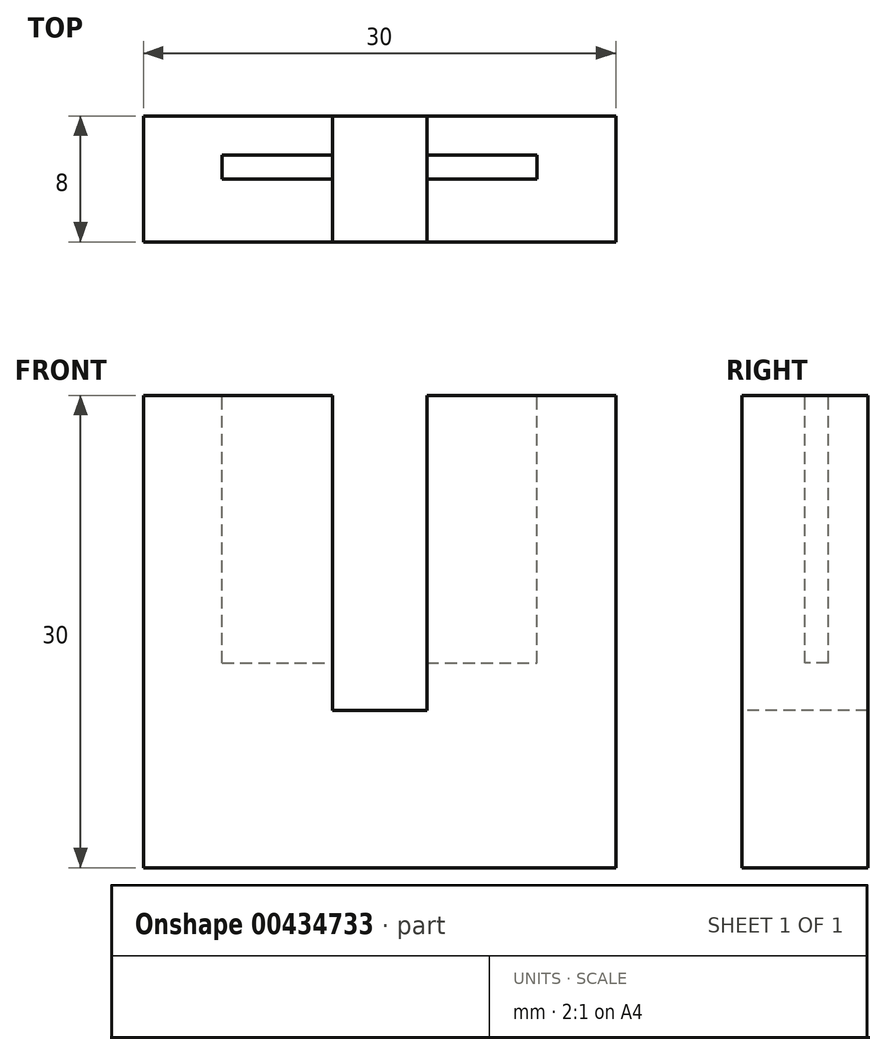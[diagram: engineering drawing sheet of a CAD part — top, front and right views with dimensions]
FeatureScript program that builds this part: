
annotation { "Feature Type Name" : "Feature", "Feature Type Description" : "" }
export const myFeature = defineFeature(function(context is Context, id is Id, definition is map)
    precondition{}
    {
        {
            var Q0;
            Q0=qCreatedBy(makeId("Top.planeOp"),FACE);
            var sketch = newSketch(context, id + "F0", { "sketchPlane" : qUnion([Q0])});
            skLineSegment(sketch, "E0.bottom", {"start": v(0, 0) * mm, "end": v(-30, 0) * mm});
            skLineSegment(sketch, "E0.top", {"start": v(0, -8) * mm, "end": v(-30, -8) * mm});
            skLineSegment(sketch, "E0.left", {"start": v(0, 0) * mm, "end": v(0, -8) * mm});
            skLineSegment(sketch, "E0.right", {"start": v(-30, 0) * mm, "end": v(-30, -8) * mm});
            skSolve(sketch);
        }
        {
            var Q0;
            Q0=makeQuery(id+"F0.imprint","IMPRINT",FACE,{"disambiguationData":[TD([[makeQuery(id+"F0.imprint","IMPRINT",EDGE,{"derivedFrom":sQuery(id+"F0.wireOp",EDGE,"E0.bottom")}),1.0]])]});
            extrude(context, id + "F1", {"entities" : qUnion([Q0]), "depth" : 30 * mm});
        }
        {
            var Q0;
            Q0=makeQuery(id+"F1.opExtrude","CAP_FACE",FACE,{"disambiguationData":[OSD([sQuery(id+"F0.wireOp",EDGE,"E0.bottom"),sQuery(id+"F0.wireOp",EDGE,"E0.top"),sQuery(id+"F0.wireOp",EDGE,"E0.left"),sQuery(id+"F0.wireOp",EDGE,"E0.right")])],"isStart":false});
            var sketch = newSketch(context, id + "F2", { "sketchPlane" : qUnion([Q0])});
            skLineSegment(sketch, "E1.bottom", {"start": v(-25, -2.5) * mm, "end": v(-5, -2.5) * mm});
            skLineSegment(sketch, "E1.top", {"start": v(-25, -4) * mm, "end": v(-5, -4) * mm});
            skLineSegment(sketch, "E1.left", {"start": v(-25, -2.5) * mm, "end": v(-25, -4) * mm});
            skLineSegment(sketch, "E1.right", {"start": v(-5, -2.5) * mm, "end": v(-5, -4) * mm});
            skSolve(sketch);
        }
        {
            var Q0;
            Q0=makeQuery(id+"F2.imprint","IMPRINT",FACE,{"disambiguationData":[TD([[makeQuery(id+"F2.imprint","IMPRINT",EDGE,{"derivedFrom":sQuery(id+"F2.wireOp",EDGE,"E1.bottom")}),1.0]])]});
            var sketch = newSketch(context, id + "F3", { "sketchPlane" : qUnion([Q0])});
            skLineSegment(sketch, "E2.bottom", {"start": v(-18, 0) * mm, "end": v(-12, 0) * mm});
            skLineSegment(sketch, "E2.top", {"start": v(-18, -8) * mm, "end": v(-12, -8) * mm});
            skLineSegment(sketch, "E2.left", {"start": v(-18, 0) * mm, "end": v(-18, -8) * mm});
            skLineSegment(sketch, "E2.right", {"start": v(-12, 0) * mm, "end": v(-12, -8) * mm});
            skSolve(sketch);
        }
        {
            var Q0;
            {var subQ0=sQuery(id+"F3.wireOp",EDGE,"E2.bottom");Q0=makeQuery(id+"F3.imprint","IMPRINT",FACE,{"disambiguationData":[TD([[makeQuery(id+"F3.imprint","IMPRINT",EDGE,{"derivedFrom":subQ0}),1.0]])]});}
            var Q1;
            {var subQ0=sQuery(id+"F3.wireOp",EDGE,"E2.left");var subQ1=makeQuery(id+"F2.imprint","IMPRINT",EDGE,{"derivedFrom":sQuery(id+"F2.wireOp",EDGE,"E1.bottom")});var subQ2=makeQuery(id+"F3.imprint","INTERSECT",VERTEX,{"derivedFrom":[subQ1,subQ0]});Q1=makeQuery(id+"F3.imprint","IMPRINT",FACE,{"disambiguationData":[TD([[makeQuery(id+"F3.imprint","IMPRINT",EDGE,{"disambiguationData":[TD([[subQ2,-1.0]])],"derivedFrom":subQ0}),1.0]])]});}
            var Q2;
            {var subQ0=sQuery(id+"F3.wireOp",EDGE,"E2.top");Q2=makeQuery(id+"F3.imprint","IMPRINT",FACE,{"disambiguationData":[TD([[makeQuery(id+"F3.imprint","IMPRINT",EDGE,{"derivedFrom":subQ0}),-1.0]])]});}
            extrude(context, id + "F4", {"entities" : qUnion([Q0, Q1, Q2]), "operationType" : NewBodyOperationType.REMOVE, "oppositeDirection" : true, "depth" : 20 * mm});
        }
        {
            var Q0;
            Q0=makeQuery(id+"F2.imprint","IMPRINT",FACE,{"disambiguationData":[TD([[makeQuery(id+"F2.imprint","IMPRINT",EDGE,{"derivedFrom":sQuery(id+"F2.wireOp",EDGE,"E1.bottom")}),-1.0]])]});
            extrude(context, id + "F5", {"entities" : qUnion([Q0]), "operationType" : NewBodyOperationType.REMOVE, "oppositeDirection" : true, "depth" : 20 * mm});
        }
        {
            var Q0;
            Q0=makeQuery(id+"F5.boolean.opBoolean","MERGE",FACE,{"derivedFrom":[makeQuery(id+"F4.boolean.opBoolean","COPY",FACE,{"derivedFrom":makeQuery(id+"F4.opExtrude","CAP_FACE",FACE,{"disambiguationData":[OSD([sQuery(id+"F3.wireOp",EDGE,"E2.bottom"),sQuery(id+"F3.wireOp",EDGE,"E2.top"),sQuery(id+"F3.wireOp",EDGE,"E2.left"),sQuery(id+"F3.wireOp",EDGE,"E2.right")])],"isStart":false})}),makeQuery(id+"F5.opExtrude","CAP_FACE",FACE,{"disambiguationData":[OSD([sQuery(id+"F2.wireOp",EDGE,"E1.bottom"),sQuery(id+"F2.wireOp",EDGE,"E1.top"),sQuery(id+"F2.wireOp",EDGE,"E1.left"),sQuery(id+"F2.wireOp",EDGE,"E1.right")])],"isStart":false})]});
            var sketch = newSketch(context, id + "F6", { "sketchPlane" : qUnion([Q0])});
            skLineSegment(sketch, "E3", {"start": v(-12, -4) * mm, "end": v(-18, -4) * mm});
            skLineSegment(sketch, "E4", {"start": v(-18, -2.5) * mm, "end": v(-12, -2.5) * mm});
            skLineSegment(sketch, "E5", {"start": v(-12, -2.5) * mm, "end": v(-12, -4) * mm});
            skLineSegment(sketch, "E6", {"start": v(-18, -2.5) * mm, "end": v(-18, -4) * mm});
            skSolve(sketch);
        }
        {
            var Q0;
            Q0=makeQuery(id+"F6.imprint","IMPRINT",FACE,{"disambiguationData":[TD([[makeQuery(id+"F6.imprint","IMPRINT",EDGE,{"derivedFrom":sQuery(id+"F6.wireOp",EDGE,"E5")}),1.0]])]});
            var Q1;
            Q1=makeQuery(id+"F6.imprint","IMPRINT",FACE,{"disambiguationData":[TD([[makeQuery(id+"F6.imprint","IMPRINT",EDGE,{"derivedFrom":sQuery(id+"F6.wireOp",EDGE,"E6")}),-1.0]])]});
            extrude(context, id + "F7", {"entities" : qUnion([Q0, Q1]), "operationType" : NewBodyOperationType.ADD, "depth" : 3 * mm});
        }
    });
